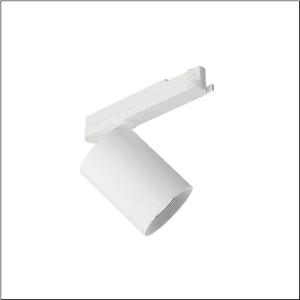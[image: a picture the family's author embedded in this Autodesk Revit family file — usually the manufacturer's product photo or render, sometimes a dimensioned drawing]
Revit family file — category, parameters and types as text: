
# Revit family: spot_21_51se12mbd5b
name_source: partatom
category: Lighting Fixtures
units: mm (PartAtom-declared; Revit-internal decimal feet)

## family parameters
Cut with Voids When Loaded = No
Host = Face
Light Source = No
Part Type = Normal
Room Calculation Point = No
Round Connector Dimension = Use Diameter
Shared = No

## types (1)
- --- (1 x LED, 5460 lm, 41.5 W, 4000K)
    Apparent Load = 42 VA
    CIE Flux Codes = 95 98 99 100 100
    Color Rendering = 90
    Color Temperature = 4000K
    Default Elevation = 1800 mm
    Description = Spot 21, directional spotlight, light control with lens, of PMMA, LED rated luminous flux: 5.250lm, light colour: 940, control gear: ECG Multilumen, with 3-phase adapter, mains connection: 220..240V, AC, 50/60Hz, of aluminium, traffic white (RAL 9016), length: 213mm, diameter: 105mm, protection rating (complete): IP20, insulation class (complete): insulation class I (protective earthing), certification: CE, impact resistance: IK02, permissible ambient temperature for indoor applications: -20..+40°C, packaging unit: 1 piece
    Height = 175 mm
    Lamp = 1 x LED
    Lamp Light Flux = 5460 lm
    Lamp Power = 41.5 W
    Lamp count = 1
    Length = 105 mm
    Luminous efficacy = 132 lm/W
    Manufacturer = Siteco
    ModVariant = No
    Model = 51SE12MBD5B
    Mounting Place = Ceiling
    Mounting Type = Pendant
    Number of Poles = 1
    OnlyDefault = Yes
    Power Factor = 1
    Product Name = Spot 21
    Product group = directional spotlight
    ProductGroupID = 905
    Protection Class = Protection class I
    Protection Degree = IP 20
    RLX_Detail_Level = 1
    RLX_Emergency_Light_Flux = 0 lm
    RLX_Emergency_Type = 0
    RLX_Emergency_Type_DB = No
    RlxData = <blob elided: 17625 chars, md5=1c7e8d9c>
    Socket = socket
    Standby Power = 0 W
    System Light Flux = 5460 lm
    System Power = 42 W
    Type Comments = factory setting: luminous flux: 100 % | (ON | ON | ON | ON) | 1050 mA
    Type Image = l_1003976.jpg
    URL = http://relux.com
    VarID = @adj_076021
    Voltage = 0 V
    Weight = 0.00 kg
    Width = 0 mm  [stored 0 ft]

note: [stored X ft] marks values corroborated as IEEE doubles in the binary element streams (Revit-internal decimal feet)

## geometry (parser evidence)
native form markers: Blend x4, Sweep x10
no freeform markers — native parametric forms only
